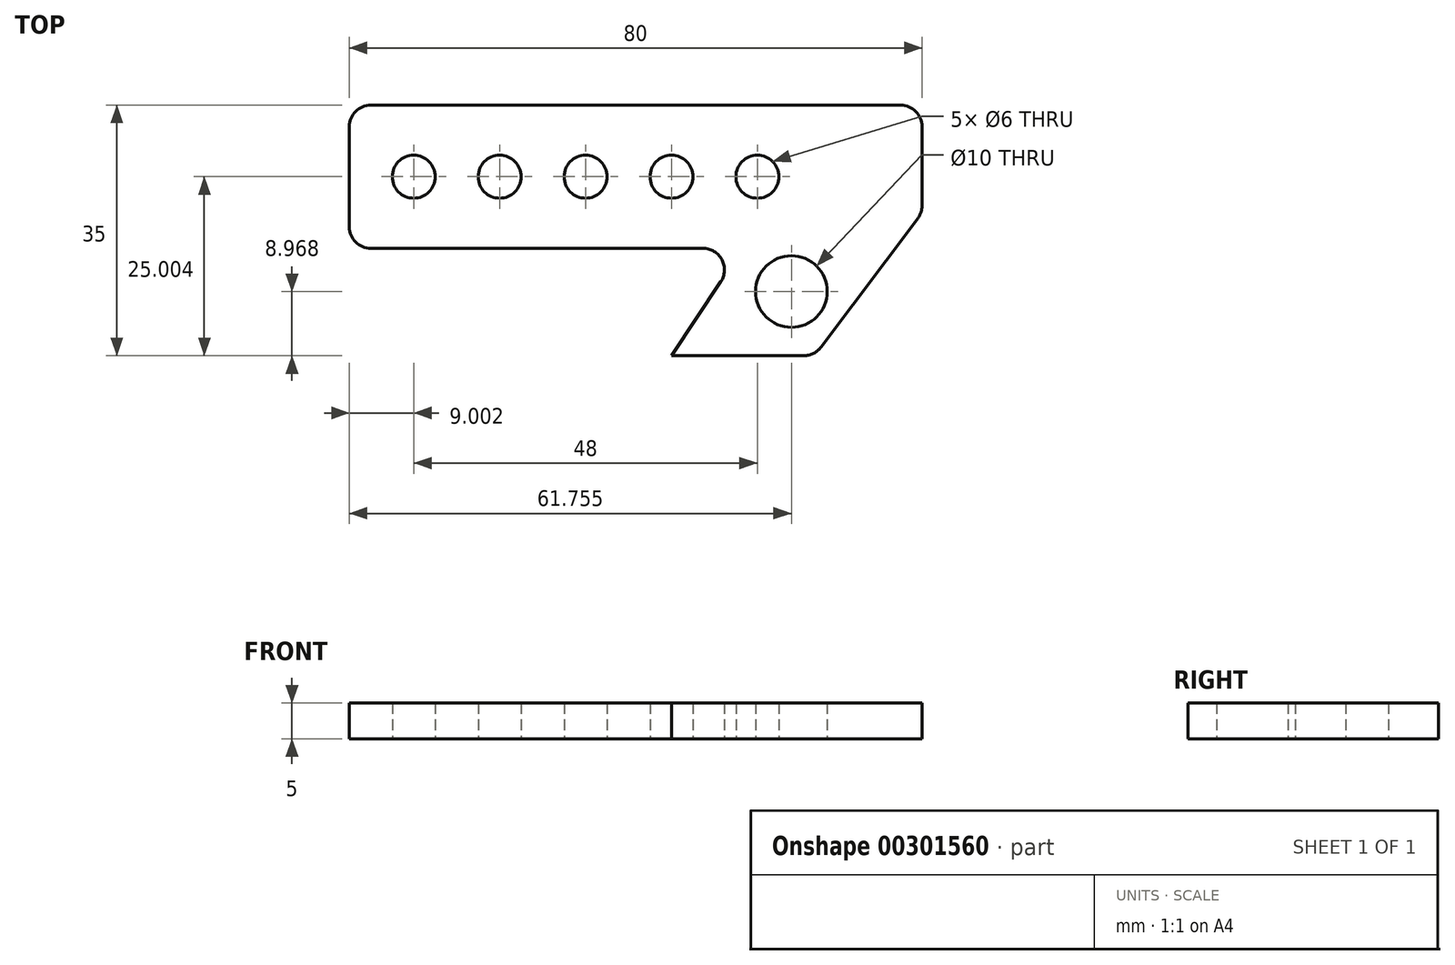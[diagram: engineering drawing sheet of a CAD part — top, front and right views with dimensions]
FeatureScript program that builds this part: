
annotation { "Feature Type Name" : "Feature", "Feature Type Description" : "" }
export const myFeature = defineFeature(function(context is Context, id is Id, definition is map)
    precondition{}
    {
        {
            var Q0;
            Q0=qCreatedBy(makeId("Top.planeOp"),FACE);
            var sketch = newSketch(context, id + "F0", { "sketchPlane" : qUnion([Q0])});
            skLineSegment(sketch, "E0", {"start": v(-58.72, 24.44) * mm, "end": v(-58.72, 38.44) * mm});
            skLineSegment(sketch, "E1", {"start": v(-55.72, 41.44) * mm, "end": v(18.28, 41.44) * mm});
            skLineSegment(sketch, "E2", {"start": v(21.28, 38.44) * mm, "end": v(21.28, 27.44) * mm});
            skLineSegment(sketch, "E3", {"start": v(-13.72, 6.44) * mm, "end": v(4.78, 6.44) * mm});
            skLineSegment(sketch, "E4", {"start": v(-55.72, 21.44) * mm, "end": v(-9.32, 21.44) * mm});
            skLineSegment(sketch, "E5", {"start": v(-13.72, 6.44) * mm, "end": v(-6.83, 16.78) * mm});
            skLineSegment(sketch, "E6", {"start": v(7.18, 7.64) * mm, "end": v(20.68, 25.64) * mm});
            skPoint(sketch, "E7.visualSharp", {"position": v(-58.72, 41.44) * mm});
            skArc(sketch, "E7.filletArc", {"start": v(-55.72, 41.44) * mm, "mid": v(-57.84, 40.57) * mm, "end": v(-58.72, 38.44) * mm});
            skPoint(sketch, "E8.visualSharp", {"position": v(-58.72, 21.44) * mm});
            skArc(sketch, "E8.filletArc", {"start": v(-58.72, 24.44) * mm, "mid": v(-57.84, 22.32) * mm, "end": v(-55.72, 21.44) * mm});
            skPoint(sketch, "E9.visualSharp", {"position": v(21.28, 41.44) * mm});
            skArc(sketch, "E9.filletArc", {"start": v(21.28, 38.44) * mm, "mid": v(20.4, 40.57) * mm, "end": v(18.28, 41.44) * mm});
            skPoint(sketch, "E10.visualSharp", {"position": v(21.28, 26.44) * mm});
            skArc(sketch, "E10.filletArc", {"start": v(20.68, 25.64) * mm, "mid": v(21.13, 26.5) * mm, "end": v(21.28, 27.44) * mm});
            skPoint(sketch, "E11.visualSharp", {"position": v(6.28, 6.44) * mm});
            skArc(sketch, "E11.filletArc", {"start": v(4.78, 6.44) * mm, "mid": v(6.12, 6.76) * mm, "end": v(7.18, 7.64) * mm});
            skPoint(sketch, "E12.visualSharp", {"position": v(-3.72, 21.44) * mm});
            skArc(sketch, "E12.filletArc", {"start": v(-6.83, 16.78) * mm, "mid": v(-6.68, 19.86) * mm, "end": v(-9.32, 21.44) * mm});
            skLineSegment(sketch, "E13", {"start": v(-58.72, 31.44) * mm, "end": v(3.3, 31.44) * mm, "construction": true});
            skCircle(sketch, "E14", {"center": v(-49.72, 31.44) * mm, "radius": 3 * mm});
            skCircle(sketch, "E15.1.0.0", {"center": v(-37.72, 31.44) * mm, "radius": 3 * mm});
            skCircle(sketch, "E15.2.0.0", {"center": v(-25.72, 31.44) * mm, "radius": 3 * mm});
            skCircle(sketch, "E15.3.0.0", {"center": v(-13.72, 31.44) * mm, "radius": 3 * mm});
            skCircle(sketch, "E15.4.0.0", {"center": v(-1.72, 31.44) * mm, "radius": 3 * mm});
            skLineSegment(sketch, "E15.direction1", {"start": v(-49.72, 31.44) * mm, "end": v(-37.72, 31.44) * mm, "construction": true});
            skLineSegment(sketch, "E16", {"start": v(-13.72, 6.44) * mm, "end": v(10.44, 19.37) * mm, "construction": true});
            skCircle(sketch, "E17", {"center": v(3.03, 15.4) * mm, "radius": 5 * mm});
            skSolve(sketch);
        }
        {
            var Q0;
            Q0=makeQuery(id+"F0.imprint","IMPRINT",FACE,{"disambiguationData":[TD([[makeQuery(id+"F0.imprint","IMPRINT",EDGE,{"derivedFrom":sQuery(id+"F0.wireOp",EDGE,"E0")}),-1.0]])]});
            extrude(context, id + "F1", {"entities" : qUnion([Q0]), "depth" : 5 * mm});
        }
    });
